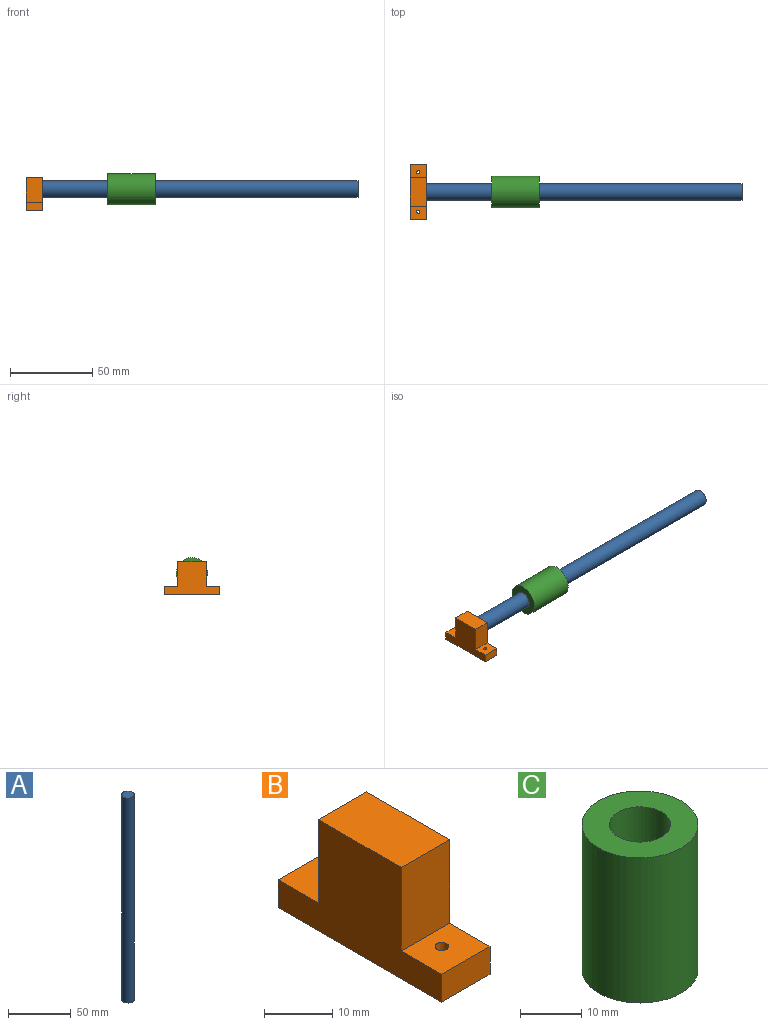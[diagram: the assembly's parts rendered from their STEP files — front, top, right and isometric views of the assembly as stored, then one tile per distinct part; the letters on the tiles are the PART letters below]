
ASSEMBLY  parts=3 mates=2
PART A: 3 faces, bbox 10x10x200 mm
  f0: cylinder r=5mm len=200mm, axis (0,0,-1), area 6283.2mm2, adj f1,f2
  f1: plane 10x10mm, normal (0,0,1), area 78.5mm2, adj f0
  f2: plane 10x10mm, normal (0,0,-1), area 78.5mm2, adj f0
PART B: 14 faces, bbox 10x34x20 mm
  f0: plane 10x8.39mm, normal (0,0,1), area 80.7mm2, adj f1,f3,f5,f6,f10
  f1: plane 34x20mm, normal (1,0,0), area 346.6mm2, adj f0,f2,f5,f7,f8,f9,f10,f11
  f2: plane 10x5mm, normal (0,1,0), area 50mm2, adj f1,f3,f7,f8
  f3: plane 34x20mm, normal (-1,0,0), area 428.4mm2, adj f0,f2,f5,f7,f8,f9,f10,f11
  f4: cylinder r=1mm len=5mm, axis (0,0,-1), area 31.4mm2, adj f7,f8
  f5: plane 10x5mm, normal (0,-1,0), area 50mm2, adj f0,f1,f3,f8
  f6: cylinder r=1mm len=5mm, axis (0,0,-1), area 31.4mm2, adj f0,f8
  f7: plane 10x8.39mm, normal (0,0,1), area 80.7mm2, adj f1,f2,f3,f4,f9
  f8: plane 34x10mm, normal (0,0,-1), area 333.7mm2, adj f1,f2,f3,f4,f5,f6
  f9: plane 15x10mm, normal (0,1,0), area 150mm2, adj f1,f3,f7,f11
  f10: plane 15x10mm, normal (0,-1,0), area 150mm2, adj f0,f1,f3,f11
  f11: plane 17.22x10mm, normal (0,0,1), area 172.2mm2, adj f1,f3,f9,f10
  f12: cylinder r=5.1mm len=10.2mm, axis (1,0,0), area 256.4mm2, adj f1,f13
  f13: plane 10.2x10.2mm, normal (1,0,0), area 81.7mm2, adj f12
PART C: 4 faces, bbox 19x19x29.1 mm
  f0: cylinder r=5mm len=29.1mm, axis (0,0,-1), area 914.2mm2, adj f2,f3
  f1: cylinder r=9.5mm len=29.1mm, axis (0,0,-1), area 1737mm2, adj f2,f3
  f2: plane 19x19mm, normal (0,0,1), area 205mm2, adj f0,f1
  f3: plane 19x19mm, normal (0,0,-1), area 205mm2, adj f0,f1
PLACE A rot(axis=(0.71,0,0.71),180deg) t=(-3,0,13)mm
PLACE B at identity fixed
PLACE C rot(axis=(0.58,0.58,0.58),120deg) t=(44.64,0,13)mm
MATE fastened B.f12 <-> A.f0  axis (1,0,0) through (-3,0,13)mm
MATE slider A.f0 <-> C.f0  axis (-1,0,0) through (97,0,13)mm
